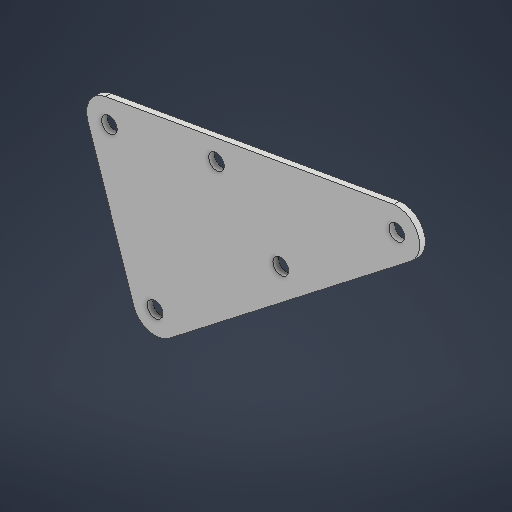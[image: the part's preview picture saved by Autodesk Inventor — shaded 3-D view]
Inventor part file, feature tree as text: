
AUTODESK INVENTOR PART (.ipt)
format: ipt  version: 2025.2 (Build 292293000, 293)  size: 190,464 bytes
history: native  units: in
note: dims shown in document units (in); Inventor stores cm internally (conversion verified against a paired STEP export)
features: extrude x1, sketch x1
ambient origin geometry x8: Origin, YZ Plane, XZ Plane, XY Plane, X Axis, Y Axis, Z Axis, Center Point
bodies: Body1 (feature_tree)
feature tree (2):
  extrude  "Extrusion2"  Depth=0.0625in TaperAngle=0.0deg
  sketch  "Sketch2"  dims[d12=0.5in d13=0.5in d14=0.5in d15=0.0625in d16=0.0in]
